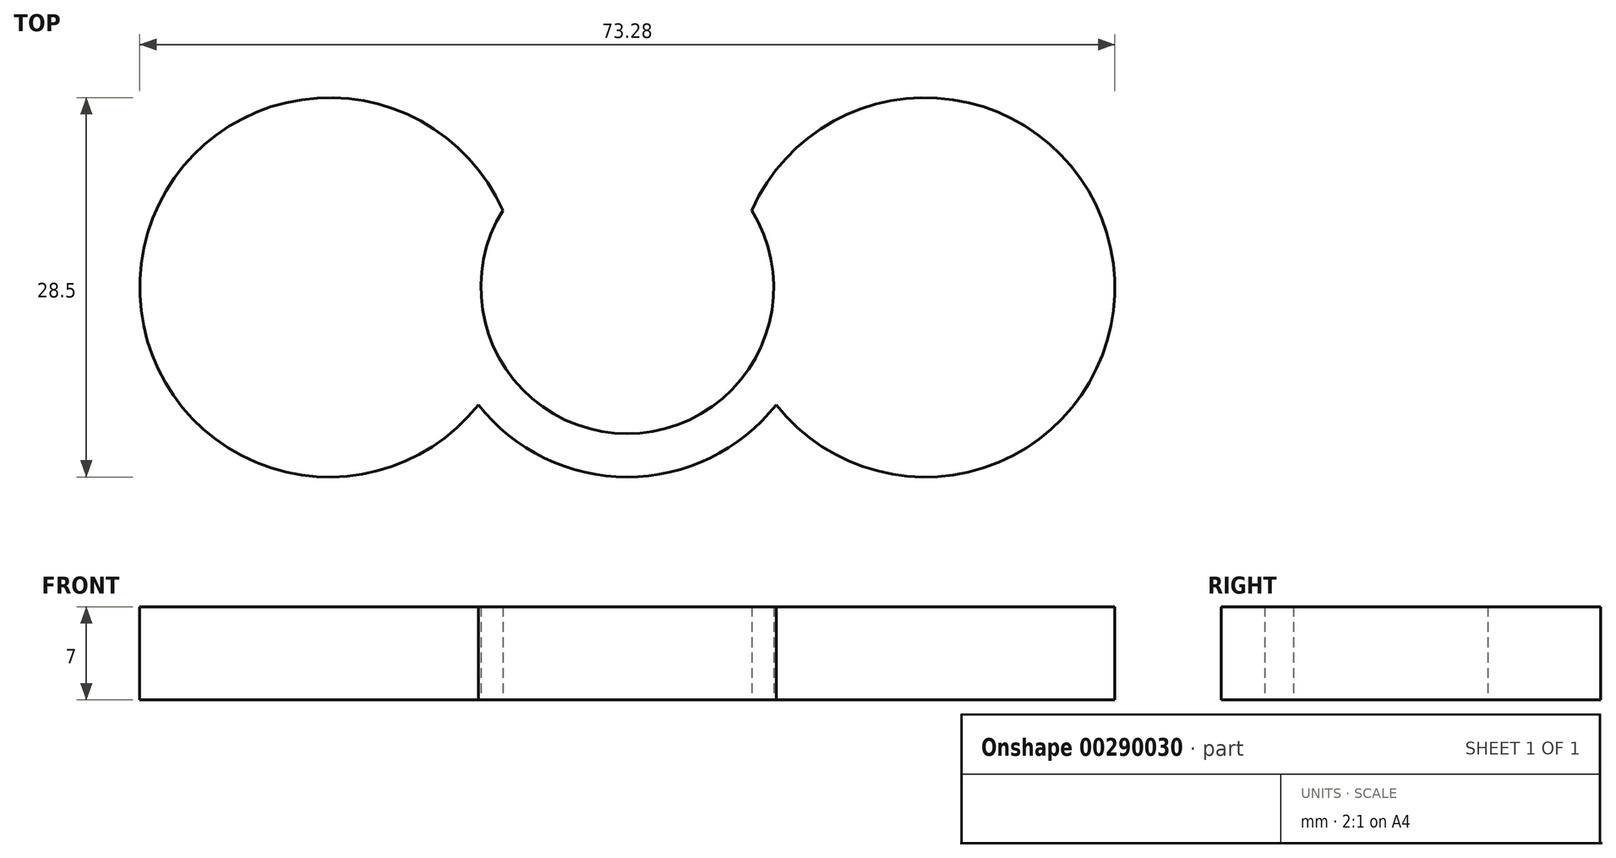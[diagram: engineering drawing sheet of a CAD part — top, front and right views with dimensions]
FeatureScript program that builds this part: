
annotation { "Feature Type Name" : "Feature", "Feature Type Description" : "" }
export const myFeature = defineFeature(function(context is Context, id is Id, definition is map)
    precondition{}
    {
        {
            var Q0;
            Q0=qCreatedBy(makeId("Top.planeOp"),FACE);
            var sketch = newSketch(context, id + "F0", { "sketchPlane" : qUnion([Q0])});
            skCircle(sketch, "E0", {"center": v(0, 0) * mm, "radius": 14.25 * mm});
            skCircle(sketch, "E1", {"center": v(22.38, 0) * mm, "radius": 14.25 * mm});
            skCircle(sketch, "E2.MirrorC", {"center": v(-22.38, 0) * mm, "radius": 14.25 * mm});
            skCircle(sketch, "E3", {"center": v(0, 0) * mm, "radius": 11 * mm});
            skSolve(sketch);
        }
        {
            var Q0;
            {var subQ0=sQuery(id+"F0.wireOp",EDGE,"E1");var subQ1=sQuery(id+"F0.wireOp",EDGE,"E0");var subQ2=makeQuery(id+"F0.imprint","INTERSECT",VERTEX,{"disambiguationData":[OD(0.0)],"derivedFrom":[subQ1,subQ0]});Q0=makeQuery(id+"F0.imprint","IMPRINT",FACE,{"disambiguationData":[TD([[makeQuery(id+"F0.imprint","IMPRINT",EDGE,{"disambiguationData":[TD([[subQ2,1.0]])],"derivedFrom":subQ1}),-1.0]])]});}
            var Q1;
            {var subQ0=sQuery(id+"F0.wireOp",EDGE,"E3");var subQ1=sQuery(id+"F0.wireOp",EDGE,"E1");var subQ2=makeQuery(id+"F0.imprint","INTERSECT",VERTEX,{"disambiguationData":[OD(0.0)],"derivedFrom":[subQ1,subQ0]});Q1=makeQuery(id+"F0.imprint","IMPRINT",FACE,{"disambiguationData":[TD([[makeQuery(id+"F0.imprint","IMPRINT",EDGE,{"disambiguationData":[TD([[subQ2,-1.0]])],"derivedFrom":subQ1}),1.0]])]});}
            var Q2;
            {var subQ0=sQuery(id+"F0.wireOp",EDGE,"E2.MirrorC");var subQ1=sQuery(id+"F0.wireOp",EDGE,"E0");var subQ2=makeQuery(id+"F0.imprint","INTERSECT",VERTEX,{"disambiguationData":[OD(0.0)],"derivedFrom":[subQ1,subQ0]});Q2=makeQuery(id+"F0.imprint","IMPRINT",FACE,{"disambiguationData":[TD([[makeQuery(id+"F0.imprint","IMPRINT",EDGE,{"disambiguationData":[TD([[subQ2,-1.0]])],"derivedFrom":subQ1}),-1.0]])]});}
            var Q3;
            {var subQ0=sQuery(id+"F0.wireOp",EDGE,"E3");var subQ1=sQuery(id+"F0.wireOp",EDGE,"E2.MirrorC");var subQ2=makeQuery(id+"F0.imprint","INTERSECT",VERTEX,{"disambiguationData":[OD(0.0)],"derivedFrom":[subQ1,subQ0]});Q3=makeQuery(id+"F0.imprint","IMPRINT",FACE,{"disambiguationData":[TD([[makeQuery(id+"F0.imprint","IMPRINT",EDGE,{"disambiguationData":[TD([[subQ2,-1.0]])],"derivedFrom":subQ1}),-1.0]])]});}
            var Q4;
            {var subQ0=sQuery(id+"F0.wireOp",EDGE,"E2.MirrorC");var subQ1=sQuery(id+"F0.wireOp",EDGE,"E0");var subQ2=makeQuery(id+"F0.imprint","INTERSECT",VERTEX,{"disambiguationData":[OD(0.0)],"derivedFrom":[subQ1,subQ0]});Q4=makeQuery(id+"F0.imprint","IMPRINT",FACE,{"disambiguationData":[TD([[makeQuery(id+"F0.imprint","IMPRINT",EDGE,{"disambiguationData":[TD([[subQ2,1.0]])],"derivedFrom":subQ1}),1.0]])]});}
            var Q5;
            {var subQ0=sQuery(id+"F0.wireOp",EDGE,"E2.MirrorC");var subQ1=sQuery(id+"F0.wireOp",EDGE,"E0");var subQ2=makeQuery(id+"F0.imprint","INTERSECT",VERTEX,{"disambiguationData":[OD(1.0)],"derivedFrom":[subQ1,subQ0]});Q5=makeQuery(id+"F0.imprint","IMPRINT",FACE,{"disambiguationData":[TD([[makeQuery(id+"F0.imprint","IMPRINT",EDGE,{"disambiguationData":[TD([[subQ2,-1.0]])],"derivedFrom":subQ1}),1.0]])]});}
            var Q6;
            {var subQ0=sQuery(id+"F0.wireOp",EDGE,"E2.MirrorC");var subQ1=sQuery(id+"F0.wireOp",EDGE,"E0");var subQ2=makeQuery(id+"F0.imprint","INTERSECT",VERTEX,{"disambiguationData":[OD(0.0)],"derivedFrom":[subQ1,subQ0]});Q6=makeQuery(id+"F0.imprint","IMPRINT",FACE,{"disambiguationData":[TD([[makeQuery(id+"F0.imprint","IMPRINT",EDGE,{"disambiguationData":[TD([[subQ2,-1.0]])],"derivedFrom":subQ1}),1.0]])]});}
            var Q7;
            {var subQ0=sQuery(id+"F0.wireOp",EDGE,"E1");var subQ1=sQuery(id+"F0.wireOp",EDGE,"E0");var subQ2=makeQuery(id+"F0.imprint","INTERSECT",VERTEX,{"disambiguationData":[OD(0.0)],"derivedFrom":[subQ1,subQ0]});Q7=makeQuery(id+"F0.imprint","IMPRINT",FACE,{"disambiguationData":[TD([[makeQuery(id+"F0.imprint","IMPRINT",EDGE,{"disambiguationData":[TD([[subQ2,1.0]])],"derivedFrom":subQ1}),1.0]])]});}
            var Q8;
            {var subQ0=sQuery(id+"F0.wireOp",EDGE,"E3");var subQ1=sQuery(id+"F0.wireOp",EDGE,"E1");var subQ2=makeQuery(id+"F0.imprint","INTERSECT",VERTEX,{"disambiguationData":[OD(0.0)],"derivedFrom":[subQ1,subQ0]});Q8=makeQuery(id+"F0.imprint","IMPRINT",FACE,{"disambiguationData":[TD([[makeQuery(id+"F0.imprint","IMPRINT",EDGE,{"disambiguationData":[TD([[subQ2,-1.0]])],"derivedFrom":subQ1}),-1.0]])]});}
            extrude(context, id + "F1", {"entities" : qUnion([Q0, Q1, Q2, Q3, Q4, Q5, Q6, Q7, Q8]), "depth" : 7 * mm});
        }
        {
            var Q0;
            {var subQ0=sQuery(id+"F0.wireOp",EDGE,"E3");var subQ1=sQuery(id+"F0.wireOp",EDGE,"E1");var subQ2=makeQuery(id+"F0.imprint","INTERSECT",VERTEX,{"disambiguationData":[OD(0.0)],"derivedFrom":[subQ1,subQ0]});Q0=makeQuery(id+"F0.imprint","IMPRINT",FACE,{"disambiguationData":[TD([[makeQuery(id+"F0.imprint","IMPRINT",EDGE,{"disambiguationData":[TD([[subQ2,-1.0]])],"derivedFrom":subQ1}),-1.0]])]});}
            var Q1;
            {var subQ0=sQuery(id+"F0.wireOp",EDGE,"E3");var subQ1=sQuery(id+"F0.wireOp",EDGE,"E2.MirrorC");var subQ2=makeQuery(id+"F0.imprint","INTERSECT",VERTEX,{"disambiguationData":[OD(0.0)],"derivedFrom":[subQ1,subQ0]});Q1=makeQuery(id+"F0.imprint","IMPRINT",FACE,{"disambiguationData":[TD([[makeQuery(id+"F0.imprint","IMPRINT",EDGE,{"disambiguationData":[TD([[subQ2,-1.0]])],"derivedFrom":subQ1}),-1.0]])]});}
            var Q2;
            {var subQ0=sQuery(id+"F0.wireOp",EDGE,"E3");var subQ1=sQuery(id+"F0.wireOp",EDGE,"E1");var subQ2=makeQuery(id+"F0.imprint","INTERSECT",VERTEX,{"disambiguationData":[OD(0.0)],"derivedFrom":[subQ1,subQ0]});Q2=makeQuery(id+"F0.imprint","IMPRINT",FACE,{"disambiguationData":[TD([[makeQuery(id+"F0.imprint","IMPRINT",EDGE,{"disambiguationData":[TD([[subQ2,-1.0]])],"derivedFrom":subQ1}),1.0]])]});}
            extrude(context, id + "F2", {"entities" : qUnion([Q0, Q1, Q2]), "operationType" : NewBodyOperationType.REMOVE, "depth" : 25 * mm});
        }
    });
